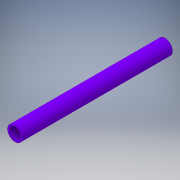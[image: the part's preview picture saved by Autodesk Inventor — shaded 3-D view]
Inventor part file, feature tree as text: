
AUTODESK INVENTOR PART (.ipt)
format: ipt  version: 2018.2 (Build 222227000, 227)  size: 106,496 bytes
history: native  units: in
note: dims shown in document units (in); Inventor stores cm internally (conversion verified against a paired STEP export)
features: extrude x1, sketch x1
ambient origin geometry x8: Origin, YZ Plane, XZ Plane, XY Plane, X Axis, Y Axis, Z Axis, Center Point
bodies: Solid1 (feature_tree)
feature tree (2):
  extrude  "Extrusion1"  Depth=13.1875in
  sketch  "Sketch1"  dims[d0=1.315in d1=1.0in d2=13.1875in d3=0.0in]
